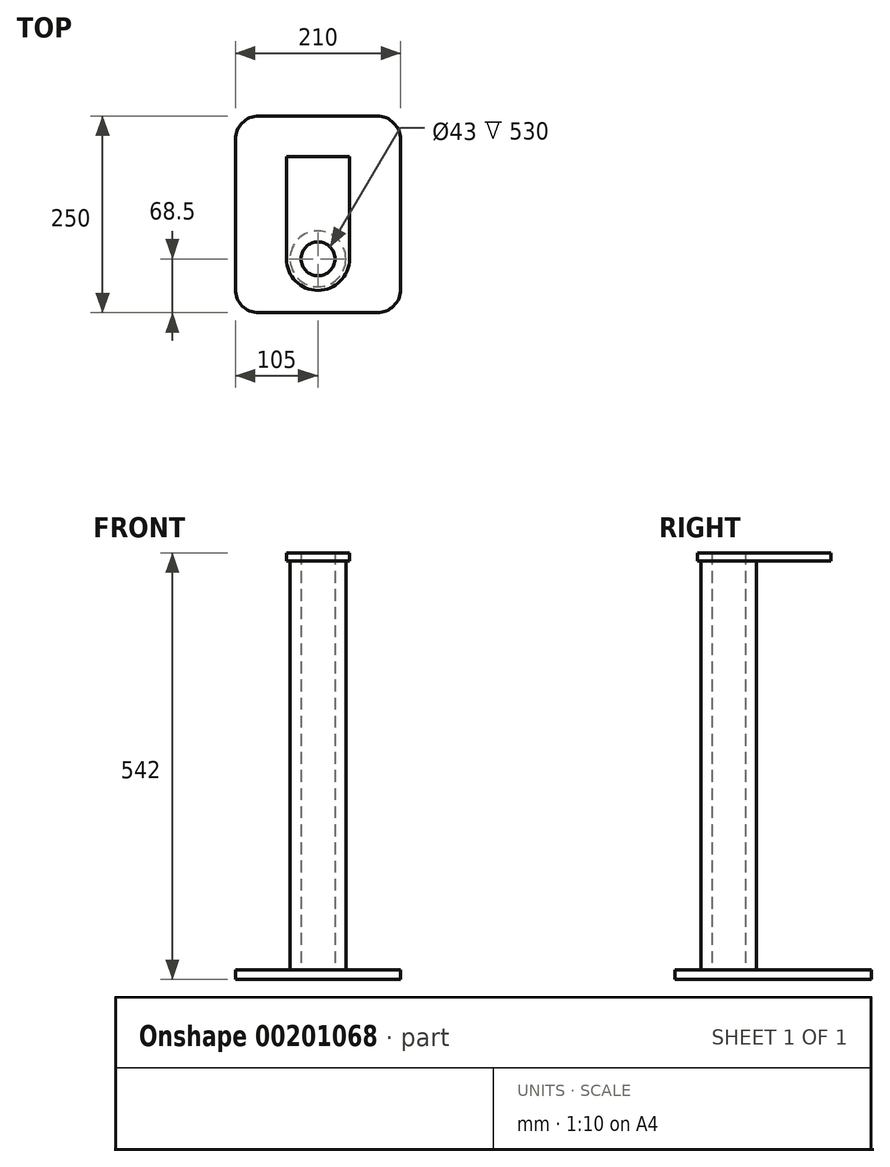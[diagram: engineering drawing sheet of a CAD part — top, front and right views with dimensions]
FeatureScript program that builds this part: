
annotation { "Feature Type Name" : "Feature", "Feature Type Description" : "" }
export const myFeature = defineFeature(function(context is Context, id is Id, definition is map)
    precondition{}
    {
        {
            var Q0;
            Q0=qCreatedBy(makeId("Top.planeOp"),FACE);
            var sketch = newSketch(context, id + "F0", { "sketchPlane" : qUnion([Q0])});
            skCircle(sketch, "E0", {"center": v(0, 0) * mm, "radius": 35.5 * mm});
            skCircle(sketch, "E1", {"center": v(0, 0) * mm, "radius": 21.5 * mm});
            skLineSegment(sketch, "E2.bottom", {"start": v(-75, 181.5) * mm, "end": v(75, 181.5) * mm});
            skLineSegment(sketch, "E2.top", {"start": v(-75, -68.5) * mm, "end": v(75, -68.5) * mm});
            skLineSegment(sketch, "E2.left", {"start": v(-105, 151.5) * mm, "end": v(-105, -38.5) * mm});
            skLineSegment(sketch, "E2.right", {"start": v(105, 151.5) * mm, "end": v(105, -38.5) * mm});
            skLineSegment(sketch, "E3", {"start": v(-105, 0) * mm, "end": v(105, 0) * mm, "construction": true});
            skPoint(sketch, "E4.visualSharp", {"position": v(-105, 181.5) * mm});
            skArc(sketch, "E4.filletArc", {"start": v(-75, 181.5) * mm, "mid": v(-96.21, 172.71) * mm, "end": v(-105, 151.5) * mm});
            skPoint(sketch, "E5.visualSharp", {"position": v(105, 181.5) * mm});
            skArc(sketch, "E5.filletArc", {"start": v(105, 151.5) * mm, "mid": v(96.21, 172.71) * mm, "end": v(75, 181.5) * mm});
            skPoint(sketch, "E6.visualSharp", {"position": v(105, -68.5) * mm});
            skArc(sketch, "E6.filletArc", {"start": v(75, -68.5) * mm, "mid": v(96.21, -59.71) * mm, "end": v(105, -38.5) * mm});
            skPoint(sketch, "E7.visualSharp", {"position": v(-105, -68.5) * mm});
            skArc(sketch, "E7.filletArc", {"start": v(-105, -38.5) * mm, "mid": v(-96.21, -59.71) * mm, "end": v(-75, -68.5) * mm});
            skSolve(sketch);
        }
        {
            var Q0;
            Q0=makeQuery(id+"F0.imprint","IMPRINT",FACE,{"disambiguationData":[TD([[makeQuery(id+"F0.imprint","IMPRINT",EDGE,{"derivedFrom":sQuery(id+"F0.wireOp",EDGE,"E0")}),-1.0]])]});
            var Q1;
            Q1=makeQuery(id+"F0.imprint","IMPRINT",FACE,{"disambiguationData":[TD([[makeQuery(id+"F0.imprint","IMPRINT",EDGE,{"derivedFrom":sQuery(id+"F0.wireOp",EDGE,"E0")}),1.0]])]});
            var Q2;
            Q2=makeQuery(id+"F0.imprint","IMPRINT",FACE,{"disambiguationData":[TD([[makeQuery(id+"F0.imprint","IMPRINT",EDGE,{"derivedFrom":sQuery(id+"F0.wireOp",EDGE,"E1")}),1.0]])]});
            extrude(context, id + "F1", {"entities" : qUnion([Q0, Q1, Q2]), "oppositeDirection" : true, "depth" : 12 * mm, "offsetDistance" : 25 * mm});
        }
        {
            var Q0;
            Q0=makeQuery(id+"F0.imprint","IMPRINT",FACE,{"disambiguationData":[TD([[makeQuery(id+"F0.imprint","IMPRINT",EDGE,{"derivedFrom":sQuery(id+"F0.wireOp",EDGE,"E0")}),1.0]])]});
            extrude(context, id + "F2", {"entities" : qUnion([Q0]), "operationType" : NewBodyOperationType.ADD, "depth" : 520 * mm, "offsetDistance" : 25 * mm});
        }
        {
            var Q0;
            Q0=makeQuery(id+"F2.opExtrude","CAP_FACE",FACE,{"disambiguationData":[OSD([sQuery(id+"F0.wireOp",EDGE,"E0"),sQuery(id+"F0.wireOp",EDGE,"E1")])],"isStart":false});
            var sketch = newSketch(context, id + "F3", { "sketchPlane" : qUnion([Q0])});
            skLineSegment(sketch, "E8.bottom", {"start": v(-40, 130) * mm, "end": v(40, 130) * mm});
            skLineSegment(sketch, "E8.top", {"start": v(-40, -40) * mm, "end": v(40, -40) * mm});
            skLineSegment(sketch, "E8.left", {"start": v(-40, 130) * mm, "end": v(-40, -40) * mm});
            skLineSegment(sketch, "E8.right", {"start": v(40, 130) * mm, "end": v(40, -40) * mm});
            skArc(sketch, "E9", {"start": v(-40, 0) * mm, "mid": v(0, -40) * mm, "end": v(40, 0) * mm});
            skSolve(sketch);
        }
        {
            var Q0;
            {var subQ4=sQuery(id+"F3.wireOp",EDGE,"E8.bottom");Q0=makeQuery(id+"F3.imprint","IMPRINT",FACE,{"disambiguationData":[TD([[makeQuery(id+"F3.imprint","IMPRINT",EDGE,{"derivedFrom":subQ4}),-1.0]])]});}
            var Q1;
            Q1=makeQuery(id+"F3.imprint","IMPRINT",FACE,{"disambiguationData":[TD([[makeQuery(id+"F3.imprint","IMPRINT",EDGE,{"derivedFrom":makeQuery(id+"F2.opExtrude","CAP_EDGE",EDGE,{"disambiguationData":[OSD([sQuery(id+"F0.wireOp",EDGE,"E0")])],"isStart":false})}),1.0]])]});
            extrude(context, id + "F4", {"entities" : qUnion([Q0, Q1]), "operationType" : NewBodyOperationType.ADD, "depth" : 10 * mm, "offsetDistance" : 25 * mm});
        }
    });
